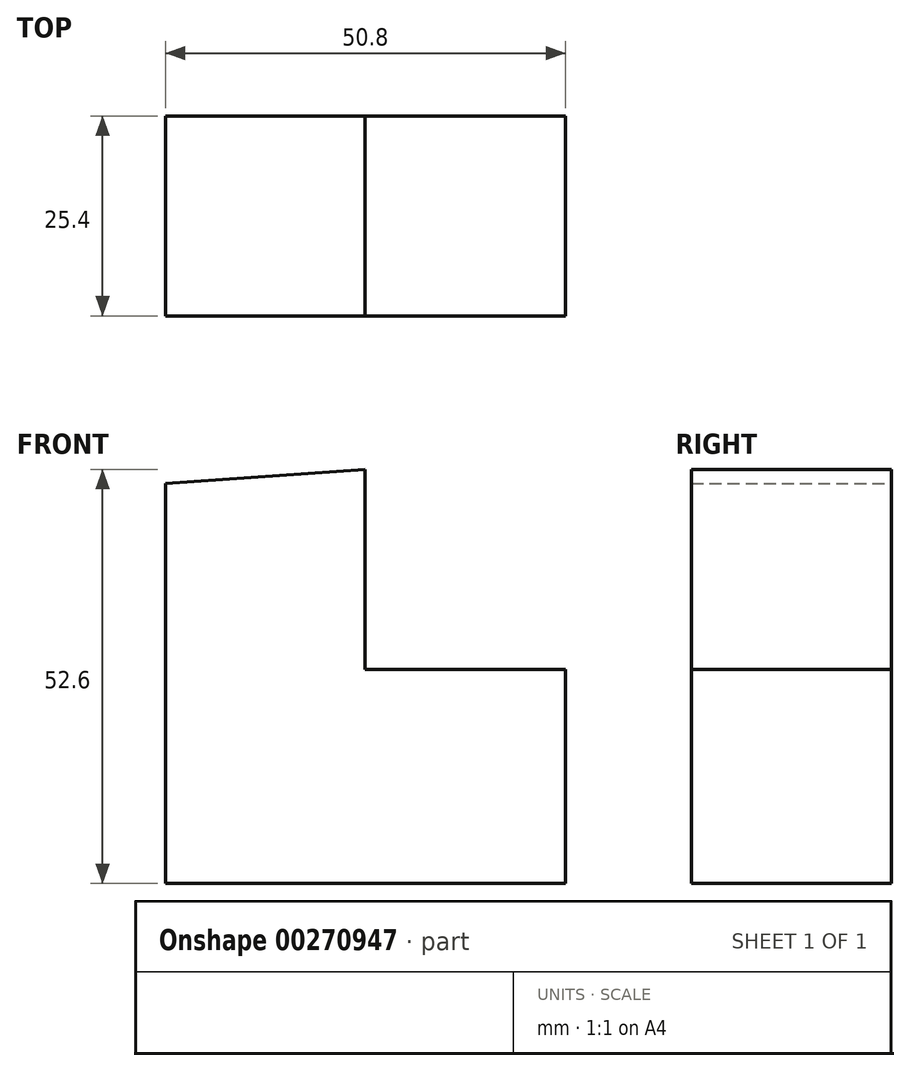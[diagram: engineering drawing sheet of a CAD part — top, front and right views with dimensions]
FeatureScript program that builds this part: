
annotation { "Feature Type Name" : "Feature", "Feature Type Description" : "" }
export const myFeature = defineFeature(function(context is Context, id is Id, definition is map)
    precondition{}
    {
        {
            var Q0;
            Q0=qCreatedBy(makeId("Front.planeOp"),FACE);
            var sketch = newSketch(context, id + "F0", { "sketchPlane" : qUnion([Q0])});
            skLineSegment(sketch, "E0", {"start": v(0, 0) * mm, "end": v(-50.8, 0) * mm});
            skLineSegment(sketch, "E1", {"start": v(-50.8, 0) * mm, "end": v(-50.8, 50.8) * mm});
            skLineSegment(sketch, "E2", {"start": v(-50.8, 50.8) * mm, "end": v(-25.46, 52.6) * mm});
            skLineSegment(sketch, "E3", {"start": v(-25.46, 52.6) * mm, "end": v(-25.46, 27.2) * mm});
            skLineSegment(sketch, "E4", {"start": v(-25.46, 27.2) * mm, "end": v(0, 27.2) * mm});
            skLineSegment(sketch, "E5", {"start": v(0, 27.2) * mm, "end": v(0, 0) * mm});
            skSolve(sketch);
        }
        {
            var Q0;
            Q0 = qSketchRegion(id + "F0", true);
            extrude(context, id + "F1", {"entities" : qUnion([Q0]), "depth" : 25.4 * mm});
        }
    });
